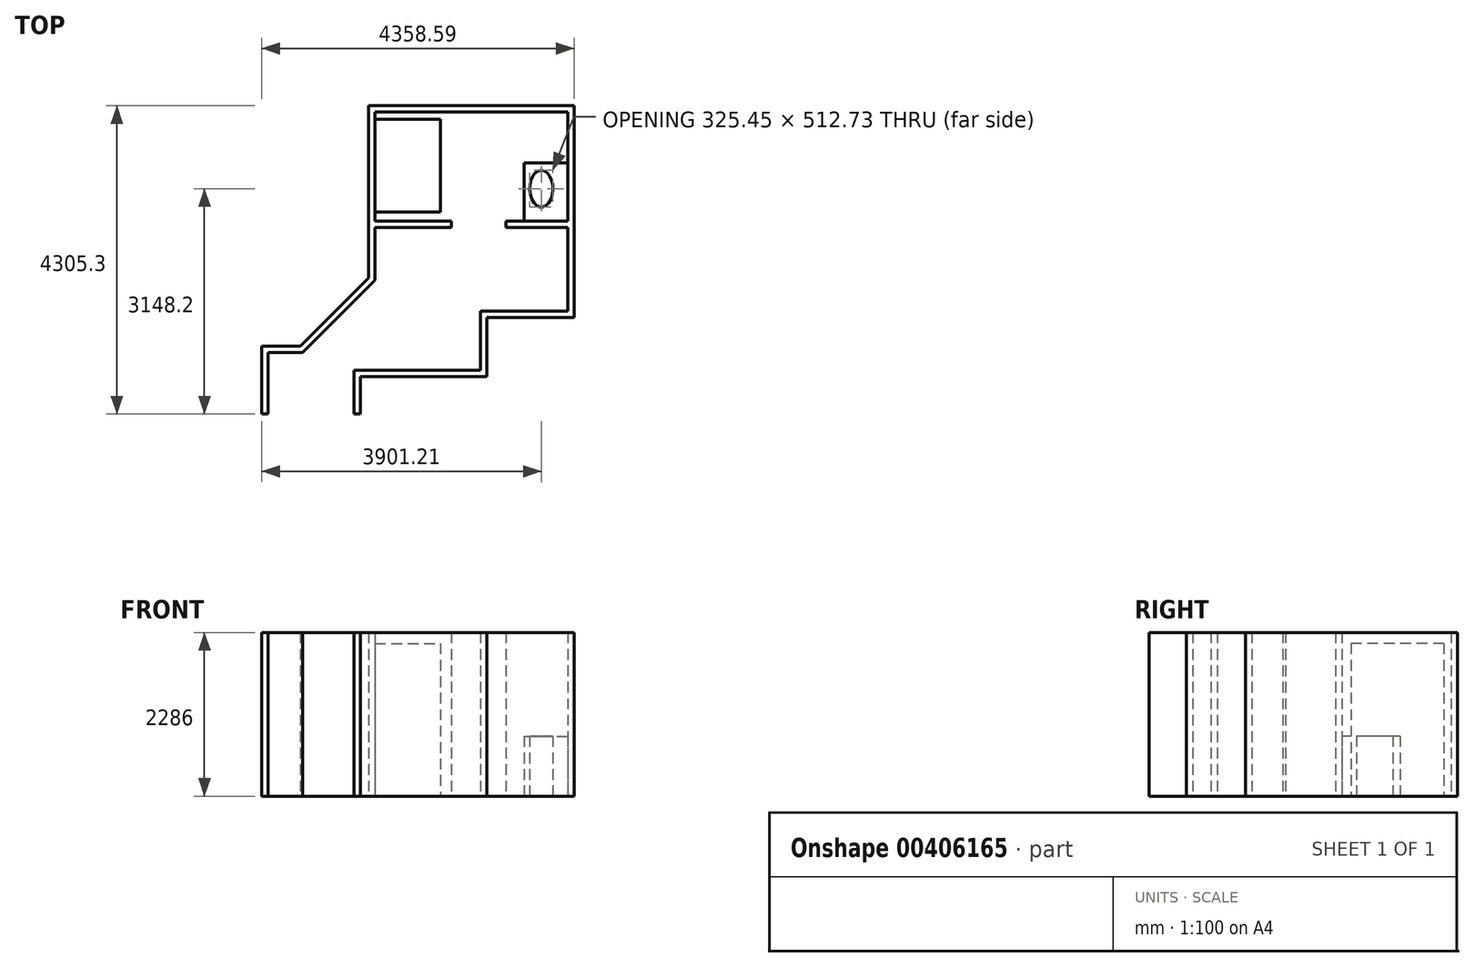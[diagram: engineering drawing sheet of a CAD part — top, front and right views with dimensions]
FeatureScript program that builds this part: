
annotation { "Feature Type Name" : "Feature", "Feature Type Description" : "" }
export const myFeature = defineFeature(function(context is Context, id is Id, definition is map)
    precondition{}
    {
        {
            var Q0;
            Q0=qCreatedBy(makeId("Top.planeOp"),FACE);
            var sketch = newSketch(context, id + "F0", { "sketchPlane" : qUnion([Q0])});
            skLineSegment(sketch, "E0", {"start": v(0, 0) * mm, "end": v(-2692.4, 0) * mm});
            skLineSegment(sketch, "E1", {"start": v(-2692.4, 0) * mm, "end": v(-2692.4, -2349.5) * mm});
            skLineSegment(sketch, "E2", {"start": v(-2692.4, -2349.5) * mm, "end": v(-3698.19, -3355.29) * mm});
            skLineSegment(sketch, "E3", {"start": v(-3698.19, -3355.29) * mm, "end": v(-4180.79, -3355.29) * mm});
            skLineSegment(sketch, "E4", {"start": v(-4180.79, -3355.29) * mm, "end": v(-4180.79, -4216.4) * mm});
            skLineSegment(sketch, "E5", {"start": v(0, 0) * mm, "end": v(0, -2781.3) * mm});
            skLineSegment(sketch, "E6", {"start": v(0, -2781.3) * mm, "end": v(-1219.2, -2781.3) * mm});
            skLineSegment(sketch, "E7", {"start": v(-1219.2, -2781.3) * mm, "end": v(-1219.2, -3606.8) * mm});
            skLineSegment(sketch, "E8", {"start": v(-1219.2, -3606.8) * mm, "end": v(-2984.5, -3606.8) * mm});
            skLineSegment(sketch, "E9", {"start": v(-2984.5, -3606.8) * mm, "end": v(-2984.5, -4216.4) * mm});
            skLineSegment(sketch, "E10.0", {"start": v(-4269.69, -3266.39) * mm, "end": v(-4269.69, -4216.4) * mm});
            skLineSegment(sketch, "E10.1", {"start": v(-3735.01, -3266.39) * mm, "end": v(-4269.69, -3266.39) * mm});
            skLineSegment(sketch, "E10.2", {"start": v(-2781.3, -2312.68) * mm, "end": v(-3735.01, -3266.39) * mm});
            skLineSegment(sketch, "E10.3", {"start": v(-2781.3, 88.9) * mm, "end": v(-2781.3, -2312.68) * mm});
            skLineSegment(sketch, "E10.4", {"start": v(88.9, 88.9) * mm, "end": v(-2781.3, 88.9) * mm});
            skLineSegment(sketch, "E10.5", {"start": v(88.9, 88.9) * mm, "end": v(88.9, -2870.2) * mm});
            skLineSegment(sketch, "E10.6", {"start": v(-2895.6, -3695.7) * mm, "end": v(-2895.6, -4216.4) * mm});
            skLineSegment(sketch, "E10.7", {"start": v(-1130.3, -3695.7) * mm, "end": v(-2895.6, -3695.7) * mm});
            skLineSegment(sketch, "E10.8", {"start": v(-1130.3, -2870.2) * mm, "end": v(-1130.3, -3695.7) * mm});
            skLineSegment(sketch, "E10.9", {"start": v(88.9, -2870.2) * mm, "end": v(-1130.3, -2870.2) * mm});
            skLineSegment(sketch, "E11", {"start": v(-4269.69, -4216.4) * mm, "end": v(-4180.79, -4216.4) * mm});
            skLineSegment(sketch, "E12", {"start": v(-2895.6, -4216.4) * mm, "end": v(-2984.5, -4216.4) * mm});
            skSolve(sketch);
        }
        {
            var Q0;
            Q0=qSketchRegion(id+"F0",true);
            extrude(context, id + "F1", {"entities" : qUnion([Q0]), "depth" : 2286 * mm});
        }
        {
            var Q0;
            Q0=qCreatedBy(makeId("Top.planeOp"),FACE);
            var sketch = newSketch(context, id + "F2", { "sketchPlane" : qUnion([Q0])});
            skLineSegment(sketch, "E13.top", {"start": v(-2692.4, -1397) * mm, "end": v(-1778, -1397) * mm});
            skLineSegment(sketch, "E13.left", {"start": v(-2692.4, -101.6) * mm, "end": v(-2692.4, -1397) * mm});
            skLineSegment(sketch, "E13.right", {"start": v(-1778, -101.6) * mm, "end": v(-1778, -1397) * mm});
            skLineSegment(sketch, "E14", {"start": v(-2692.4, -101.6) * mm, "end": v(-1778, -101.6) * mm});
            skSolve(sketch);
        }
        {
            var Q0;
            Q0=qCreatedBy(makeId("Top.planeOp"),FACE);
            var sketch = newSketch(context, id + "F3", { "sketchPlane" : qUnion([Q0])});
            skLineSegment(sketch, "E15.bottom", {"start": v(-609.6, -711.2) * mm, "end": v(0, -711.2) * mm});
            skLineSegment(sketch, "E15.top", {"start": v(-609.6, -1524) * mm, "end": v(0, -1524) * mm});
            skLineSegment(sketch, "E15.left", {"start": v(-609.6, -711.2) * mm, "end": v(-609.6, -1524) * mm});
            skLineSegment(sketch, "E15.right", {"start": v(0, -711.2) * mm, "end": v(0, -1524) * mm});
            skEllipse(sketch, "E16", {"center": v(-368.48, -1068.2) * mm, "majorRadius": 256.36 * mm, "minorRadius": 162.73 * mm, "majorAxis": v(0, 1)});
            skSolve(sketch);
        }
        {
            var Q0;
            Q0=qCreatedBy(makeId("Top.planeOp"),FACE);
            var sketch = newSketch(context, id + "F4", { "sketchPlane" : qUnion([Q0])});
            skLineSegment(sketch, "E17", {"start": v(-863.6, -1524) * mm, "end": v(0, -1524) * mm});
            skLineSegment(sketch, "E18", {"start": v(0, -1524) * mm, "end": v(0, -1612.9) * mm});
            skLineSegment(sketch, "E19", {"start": v(0, -1612.9) * mm, "end": v(-863.6, -1612.9) * mm});
            skLineSegment(sketch, "E20", {"start": v(-863.6, -1612.9) * mm, "end": v(-863.6, -1524) * mm});
            skLineSegment(sketch, "E21", {"start": v(-1625.6, -1524) * mm, "end": v(-2692.4, -1524) * mm});
            skLineSegment(sketch, "E22", {"start": v(-2692.4, -1524) * mm, "end": v(-2692.4, -1612.9) * mm});
            skLineSegment(sketch, "E23", {"start": v(-2692.4, -1612.9) * mm, "end": v(-1625.6, -1612.9) * mm});
            skLineSegment(sketch, "E24", {"start": v(-1625.6, -1612.9) * mm, "end": v(-1625.6, -1524) * mm});
            skArc(sketch, "E25", {"start": v(-1625.6, -1612.9) * mm, "mid": v(-1402.42, -2151.72) * mm, "end": v(-863.6, -2374.9) * mm, "construction": true});
            skLineSegment(sketch, "E26", {"start": v(-863.6, -1612.9) * mm, "end": v(-863.6, -2374.9) * mm, "construction": true});
            skSolve(sketch);
        }
        {
            var Q0;
            Q0 = qSketchRegion(id + "F4", true);
            extrude(context, id + "F5", {"entities" : qUnion([Q0]), "operationType" : NewBodyOperationType.ADD, "depth" : 2286 * mm});
        }
        {
            var Q0;
            Q0 = qSketchRegion(id + "F2", true);
            extrude(context, id + "F6", {"entities" : qUnion([Q0]), "operationType" : NewBodyOperationType.ADD, "depth" : 2133.6 * mm});
        }
        {
            var Q0;
            Q0 = qSketchRegion(id + "F3", true);
            extrude(context, id + "F7", {"entities" : qUnion([Q0]), "operationType" : NewBodyOperationType.ADD, "depth" : 838.2 * mm});
        }
    });
